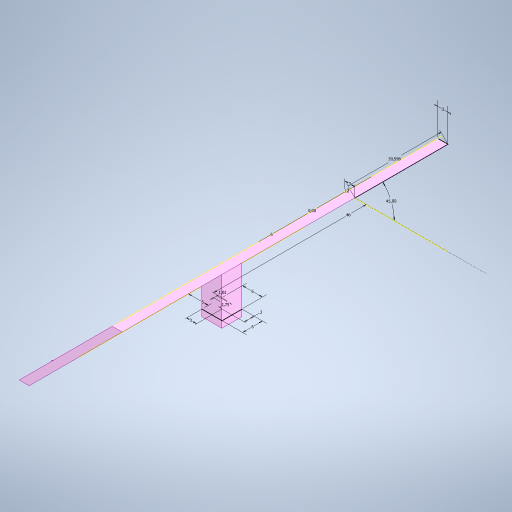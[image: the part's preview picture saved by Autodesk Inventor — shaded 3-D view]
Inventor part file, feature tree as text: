
AUTODESK INVENTOR PART (.ipt)
format: ipt  version: 2023 (Build 270158000, 158)  size: 357,888 bytes
history: native  units: in
note: dims shown in document units (in); Inventor stores cm internally (conversion verified against a paired STEP export)
features: extrude x4, sketch x3, hole x2, other x1, revolve x1, chamfer x1
ambient origin geometry x8: Origin, YZ Plane, XZ Plane, XY Plane, X Axis, Y Axis, Z Axis, Center Point
bodies: Body1 (feature_tree)
feature tree (12):
  other  "Bryła1"
  sketch  "Szkic1"
  extrude  "Wyciągnięcie proste1"  Depth=1.559in
  sketch  "Szkic2"
  revolve  "Revolution3"  Angle=45.0deg
  sketch  "Sketch3"  dims[d0=0.1181in d1=1.559in d2=45.0deg d3=0.1181in d4=3.8583in d5=0.0in d12=1.2368in d13=0.2362in d14=0.4724in d15=0.1181in d16=0.962in d17=0.2362in d18=0.2362in d19=0.2362in d20=1.811in d21=0.1181in d22=0.1181in d23=0.1083in d24=0.0398in d25=0.5906in d26=0.0in d27=0.2362in d28=0.0in d29=0.2362in d30=0.0787in d31=45.0deg d32=0.126in d33=0.2362in d34=0.248in d35=0.0787in d36=90.0deg d37=1.1811in d38=0.0in d39=0.0787in d40=0.0in d41=0.126in d42=0.2362in d43=0.2559in d44=0.0945in d45=90.0deg d46=1.1811in d47=0.0in d10=0.0197in d11=0.0344in]
  extrude  "Extrusion2"  Depth=0.1181in
  extrude  "Extrusion3"  Depth=3.8583in TaperAngle=0.0deg
  chamfer  "Chamfer1"  Distance=1.2368in
  hole  "Hole1"  [1 undecoded]
  extrude  "Extrusion4"  Depth=0.4724in
  hole  "Hole2"  [1 undecoded]
note: 2 required parameter values undecoded (feature->parameter linkage not recoverable at this tier; creation-order binding heuristic only, values carry confidence <= 0.55)
